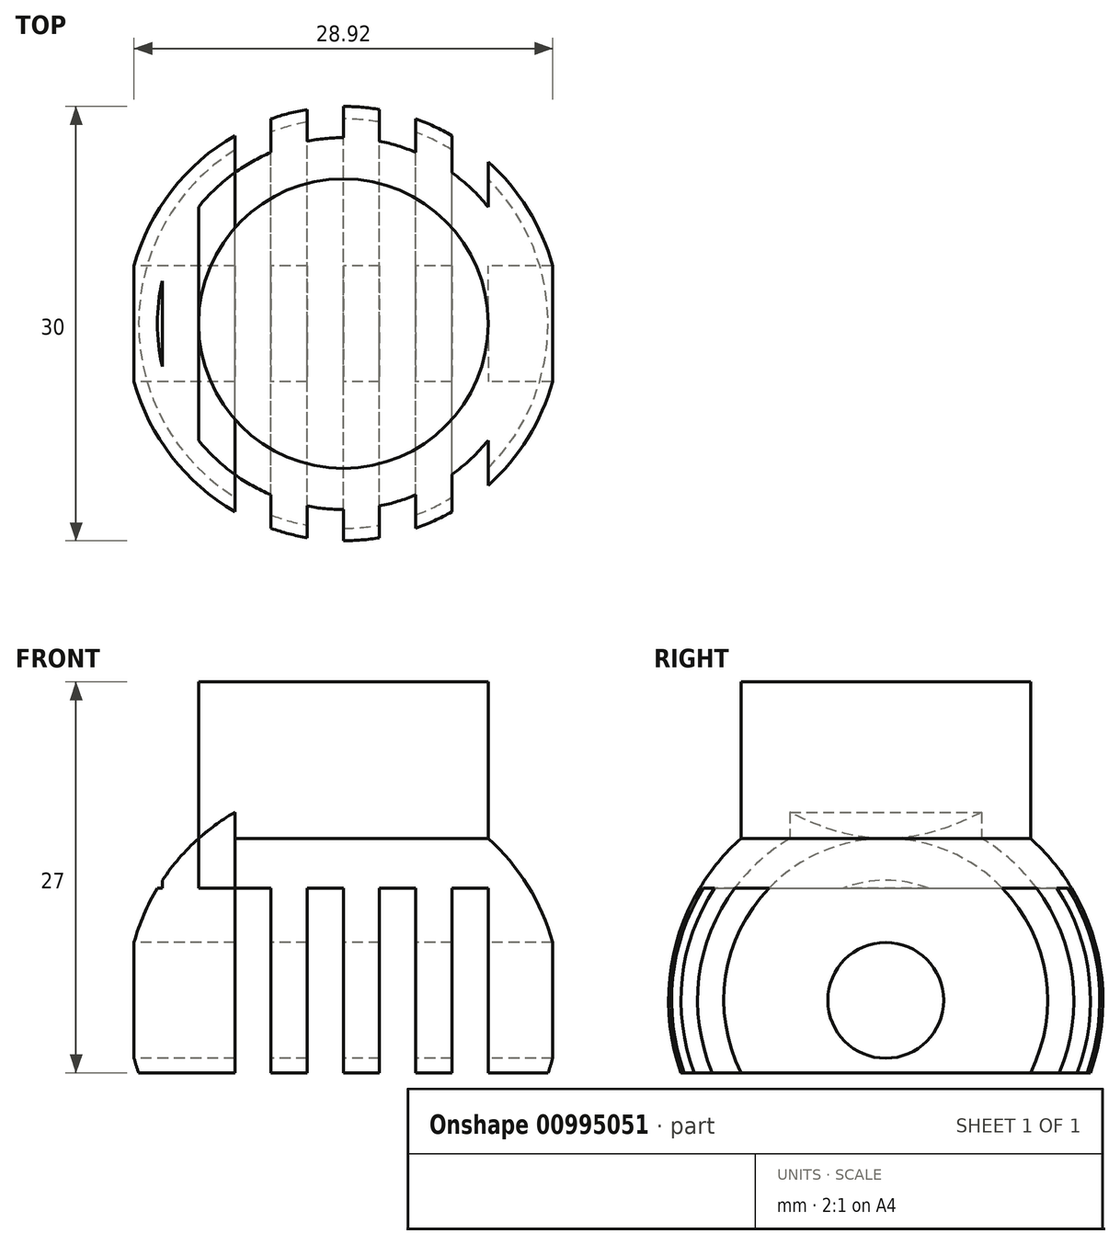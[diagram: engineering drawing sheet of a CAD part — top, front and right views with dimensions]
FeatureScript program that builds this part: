
annotation { "Feature Type Name" : "Feature", "Feature Type Description" : "" }
export const myFeature = defineFeature(function(context is Context, id is Id, definition is map)
    precondition{}
    {
        {
            var Q0;
            Q0=qCreatedBy(makeId("Front.planeOp"),FACE);
            var sketch = newSketch(context, id + "F0", { "sketchPlane" : qUnion([Q0])});
            skArc(sketch, "E0", {"start": v(0, 15) * mm, "mid": v(-15, 0) * mm, "end": v(0, -15) * mm});
            skLineSegment(sketch, "E1.bottom", {"start": v(0, 15) * mm, "end": v(-10, 15) * mm});
            skLineSegment(sketch, "E1.top", {"start": v(0, 22) * mm, "end": v(-10, 22) * mm});
            skLineSegment(sketch, "E1.left", {"start": v(0, 15) * mm, "end": v(0, 22) * mm});
            skLineSegment(sketch, "E1.right", {"start": v(-10, 15) * mm, "end": v(-10, 22) * mm});
            skLineSegment(sketch, "E2", {"start": v(-10, 15) * mm, "end": v(-10, 11.18) * mm});
            skLineSegment(sketch, "E3", {"start": v(0, 15) * mm, "end": v(0, -15) * mm});
            skLineSegment(sketch, "E4", {"start": v(-14.14, -5) * mm, "end": v(0, -5) * mm});
            skSolve(sketch);
        }
        {
            var Q0;
            {var subQ4=sQuery(id+"F0.wireOp",EDGE,"E4");Q0=makeQuery(id+"F0.imprint","IMPRINT",FACE,{"disambiguationData":[TD([[makeQuery(id+"F0.imprint","IMPRINT",EDGE,{"derivedFrom":subQ4}),1.0]])]});}
            var Q1;
            {var subQ0=sQuery(id+"F0.wireOp",EDGE,"E1.bottom");Q1=makeQuery(id+"F0.imprint","IMPRINT",FACE,{"disambiguationData":[TD([[makeQuery(id+"F0.imprint","IMPRINT",EDGE,{"derivedFrom":subQ0}),1.0]])]});}
            var Q2;
            Q2=makeQuery(id+"F0.imprint","IMPRINT",FACE,{"disambiguationData":[TD([[makeQuery(id+"F0.imprint","IMPRINT",EDGE,{"derivedFrom":sQuery(id+"F0.wireOp",EDGE,"E1.bottom")}),-1.0]])]});
            var Q3;
            Q3=sQuery(id+"F0.wireOp",EDGE,"E1.left");
            revolve(context, id + "F1", {"surfaceOperationType" : NewSurfaceOperationType.NEW, "entities" : qUnion([Q0, Q1, Q2]), "axis" : qUnion([Q3]), "revolveType" : RevolveType.FULL});
        }
        {
            var Q0;
            Q0=qCreatedBy(makeId("Front.planeOp"),FACE);
            var sketch = newSketch(context, id + "F2", { "sketchPlane" : qUnion([Q0])});
            skArc(sketch, "E5", {"start": v(14.95, 1.26) * mm, "mid": v(0, 15) * mm, "end": v(-14.95, 1.26) * mm});
            skLineSegment(sketch, "E6", {"start": v(0, -15) * mm, "end": v(0, -50.42) * mm});
            skLineSegment(sketch, "E7", {"start": v(0, -15) * mm, "end": v(0, 0) * mm});
            skSolve(sketch);
        }
        {
            var Q0;
            Q0=qCreatedBy(makeId("Top.planeOp"),FACE);
            var sketch = newSketch(context, id + "F3", { "sketchPlane" : qUnion([Q0])});
            skCircle(sketch, "E8", {"center": v(0, 0) * mm, "radius": 15 * mm});
            skLineSegment(sketch, "E9", {"start": v(0, 0) * mm, "end": v(0, 15) * mm});
            skLineSegment(sketch, "E10", {"start": v(0, 15) * mm, "end": v(0, 50.34) * mm});
            skSolve(sketch);
        }
        {
            var Q0;
            Q0=sQuery(id+"F3.wireOp",VERTEX,"E9.end");
            var Q1;
            Q1=sQuery(id+"F3.wireOp",EDGE,"E10");
            cPlane(context, id + "F4", {"entities" : qUnion([Q0, Q1]), "cplaneType" : CPlaneType.LINE_POINT, "offset" : 25 * mm, "width" : 150 * mm, "height" : 150 * mm});
        }
        {
            var Q0;
            Q0=qCreatedBy(id+"F4.planeOp",FACE);
            var sketch = newSketch(context, id + "F5", { "sketchPlane" : qUnion([Q0])});
            skArc(sketch, "E11", {"start": v(-6, 13.75) * mm, "mid": v(0, -15) * mm, "end": v(6, 13.75) * mm});
            skLineSegment(sketch, "E12", {"start": v(6, 13.75) * mm, "end": v(-6, 13.75) * mm});
            skLineSegment(sketch, "E13", {"start": v(0, 13.75) * mm, "end": v(0, -15) * mm});
            skLineSegment(sketch, "E14.1.0.0", {"start": v(2.5, 13.75) * mm, "end": v(2.5, -15) * mm});
            skLineSegment(sketch, "E14.2.0.0", {"start": v(5, 13.75) * mm, "end": v(5, -15) * mm});
            skLineSegment(sketch, "E14.3.0.0", {"start": v(7.5, 13.75) * mm, "end": v(7.5, -15) * mm});
            skLineSegment(sketch, "E14.4.0.0", {"start": v(10, 13.75) * mm, "end": v(10, -15) * mm});
            skLineSegment(sketch, "E14.5.0.0", {"start": v(12.5, 13.75) * mm, "end": v(12.5, -15) * mm});
            skLineSegment(sketch, "E14.direction1", {"start": v(0, -15) * mm, "end": v(2.5, -15) * mm, "construction": true});
            skLineSegment(sketch, "E15.MirrorCS", {"start": v(-2.5, 13.75) * mm, "end": v(-2.5, -15) * mm});
            skLineSegment(sketch, "E16.MirrorCS", {"start": v(-5, 13.75) * mm, "end": v(-5, -15) * mm});
            skLineSegment(sketch, "E17.MirrorCS", {"start": v(-7.5, 13.75) * mm, "end": v(-7.5, -15) * mm});
            skLineSegment(sketch, "E18.MirrorCS", {"start": v(-10, 13.75) * mm, "end": v(-10, -15) * mm});
            skLineSegment(sketch, "E19.MirrorCS", {"start": v(-12.5, 13.75) * mm, "end": v(-12.5, -15) * mm});
            skLineSegment(sketch, "E20", {"start": v(12.84, 7.75) * mm, "end": v(-12.84, 7.75) * mm});
            skSolve(sketch);
        }
        {
            var Q0;
            {var subQ0=sQuery(id+"F5.wireOp",EDGE,"E14.4.0.0");var subQ1=sQuery(id+"F5.wireOp",EDGE,"E11");var subQ2=makeQuery(id+"F5.imprint","INTERSECT",VERTEX,{"disambiguationData":[OD(0.0)],"derivedFrom":[subQ1,subQ0]});Q0=makeQuery(id+"F5.imprint","IMPRINT",FACE,{"disambiguationData":[TD([[makeQuery(id+"F5.imprint","IMPRINT",EDGE,{"disambiguationData":[TD([[subQ2,-1.0]])],"derivedFrom":subQ1}),1.0]])]});}
            var Q1;
            {var subQ0=sQuery(id+"F5.wireOp",EDGE,"E14.2.0.0");var subQ1=sQuery(id+"F5.wireOp",EDGE,"E11");var subQ2=makeQuery(id+"F5.imprint","INTERSECT",VERTEX,{"derivedFrom":[subQ1,subQ0]});Q1=makeQuery(id+"F5.imprint","IMPRINT",FACE,{"disambiguationData":[TD([[makeQuery(id+"F5.imprint","IMPRINT",EDGE,{"disambiguationData":[TD([[subQ2,-1.0]])],"derivedFrom":subQ1}),1.0]])]});}
            var Q2;
            {var subQ0=sQuery(id+"F5.wireOp",EDGE,"E13");var subQ1=sQuery(id+"F5.wireOp",EDGE,"E11");var subQ2=makeQuery(id+"F5.imprint","INTERSECT",VERTEX,{"derivedFrom":[subQ1,subQ0]});Q2=makeQuery(id+"F5.imprint","IMPRINT",FACE,{"disambiguationData":[TD([[makeQuery(id+"F5.imprint","IMPRINT",EDGE,{"disambiguationData":[TD([[subQ2,-1.0]])],"derivedFrom":subQ1}),1.0]])]});}
            var Q3;
            {var subQ0=sQuery(id+"F5.wireOp",EDGE,"E16.MirrorCS");var subQ1=sQuery(id+"F5.wireOp",EDGE,"E11");var subQ2=makeQuery(id+"F5.imprint","INTERSECT",VERTEX,{"derivedFrom":[subQ1,subQ0]});Q3=makeQuery(id+"F5.imprint","IMPRINT",FACE,{"disambiguationData":[TD([[makeQuery(id+"F5.imprint","IMPRINT",EDGE,{"disambiguationData":[TD([[subQ2,-1.0]])],"derivedFrom":subQ1}),1.0]])]});}
            var Q4;
            {var subQ0=sQuery(id+"F5.wireOp",EDGE,"E18.MirrorCS");var subQ1=sQuery(id+"F5.wireOp",EDGE,"E11");var subQ2=makeQuery(id+"F5.imprint","INTERSECT",VERTEX,{"disambiguationData":[OD(1.0)],"derivedFrom":[subQ1,subQ0]});Q4=makeQuery(id+"F5.imprint","IMPRINT",FACE,{"disambiguationData":[TD([[makeQuery(id+"F5.imprint","IMPRINT",EDGE,{"disambiguationData":[TD([[subQ2,-1.0]])],"derivedFrom":subQ1}),1.0]])]});}
            var Q5;
            {var subQ0=sQuery(id+"F5.wireOp",EDGE,"E20");var subQ1=sQuery(id+"F5.wireOp",EDGE,"E11");var subQ2=makeQuery(id+"F5.imprint","INTERSECT",VERTEX,{"disambiguationData":[OD(1.0)],"derivedFrom":[subQ1,subQ0]});Q5=makeQuery(id+"F5.imprint","IMPRINT",FACE,{"disambiguationData":[TD([[makeQuery(id+"F5.imprint","IMPRINT",EDGE,{"disambiguationData":[TD([[subQ2,-1.0]])],"derivedFrom":subQ1}),1.0]])]});}
            extrude(context, id + "F6", {"entities" : qUnion([Q0, Q1, Q2, Q3, Q4, Q5]), "operationType" : NewBodyOperationType.REMOVE, "endBound" : BoundingType.THROUGH_ALL, "oppositeDirection" : true, "depth" : 25 * mm, "offsetDistance" : 25 * mm});
        }
        {
            var Q0;
            Q0=qCreatedBy(makeId("Top.planeOp"),FACE);
            var sketch = newSketch(context, id + "F7", { "sketchPlane" : qUnion([Q0])});
            skLineSegment(sketch, "E21", {"start": v(0, 0) * mm, "end": v(-15, 0) * mm});
            skLineSegment(sketch, "E22", {"start": v(-15, 0) * mm, "end": v(-35.68, 0) * mm});
            skCircle(sketch, "E23.0", {"center": v(0, 0) * mm, "radius": 15 * mm});
            skSolve(sketch);
        }
        {
            var Q0;
            Q0=sQuery(id+"F7.wireOp",VERTEX,"E21.end");
            var Q1;
            Q1=sQuery(id+"F7.wireOp",EDGE,"E22");
            cPlane(context, id + "F8", {"entities" : qUnion([Q0, Q1]), "cplaneType" : CPlaneType.LINE_POINT, "offset" : 25 * mm, "width" : 150 * mm, "height" : 150 * mm});
        }
        {
            var Q0;
            Q0=qCreatedBy(id+"F8.planeOp",FACE);
            var sketch = newSketch(context, id + "F9", { "sketchPlane" : qUnion([Q0])});
            skCircle(sketch, "E24", {"center": v(0, 0) * mm, "radius": 4 * mm});
            skSolve(sketch);
        }
        {
            var Q0;
            Q0 = qSketchRegion(id + "F9", true);
            extrude(context, id + "F10", {"entities" : qUnion([Q0]), "operationType" : NewBodyOperationType.REMOVE, "endBound" : BoundingType.THROUGH_ALL, "oppositeDirection" : true, "depth" : 25 * mm, "offsetDistance" : 25 * mm});
        }
    });
